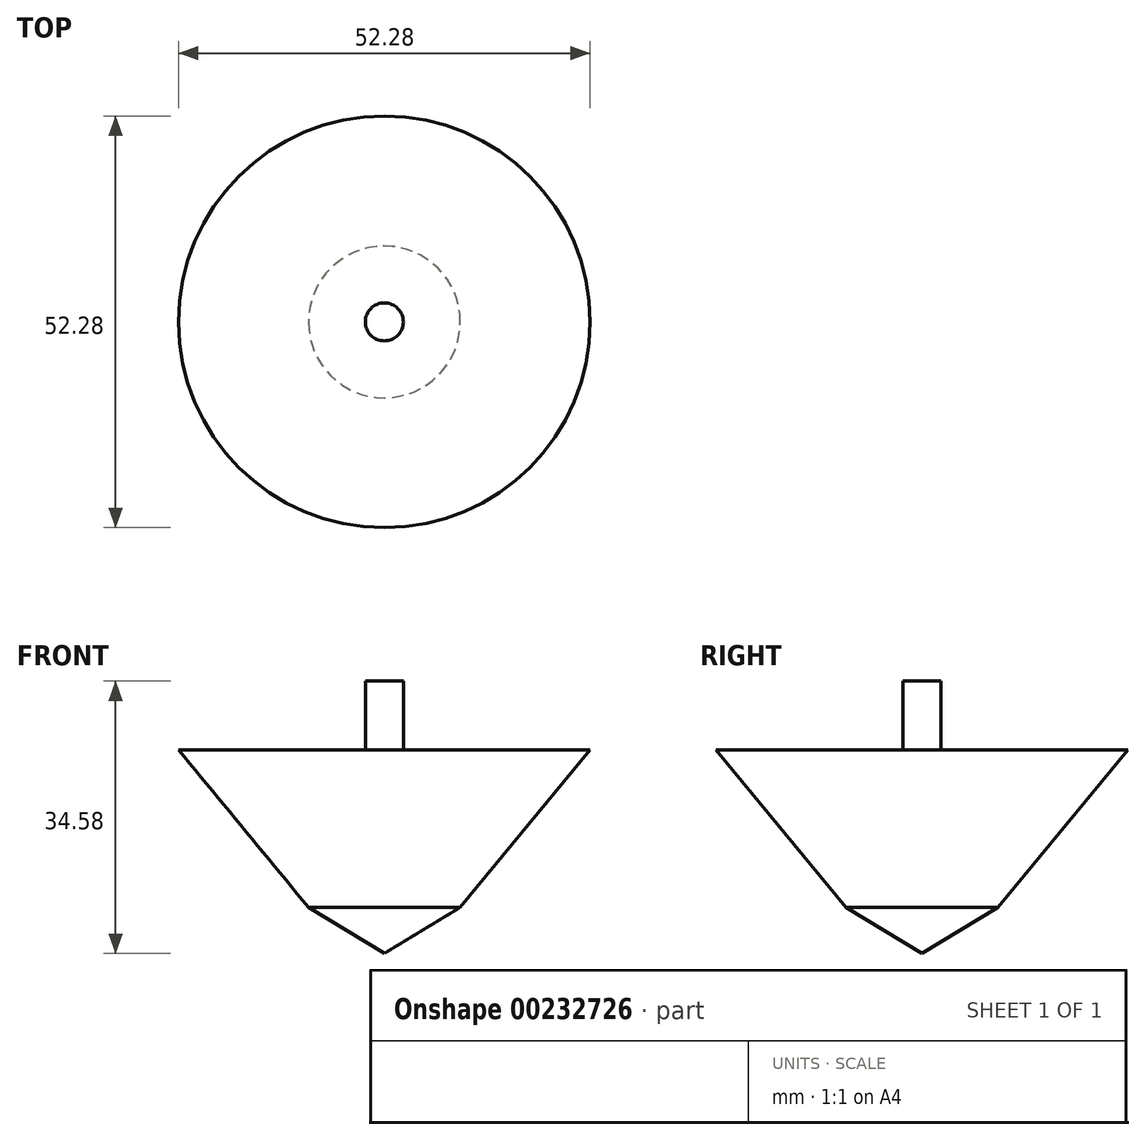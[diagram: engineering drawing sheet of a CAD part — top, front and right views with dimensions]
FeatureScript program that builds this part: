
annotation { "Feature Type Name" : "Feature", "Feature Type Description" : "" }
export const myFeature = defineFeature(function(context is Context, id is Id, definition is map)
    precondition{}
    {
        {
            var Q0;
            Q0=qCreatedBy(makeId("Front.planeOp"),FACE);
            var sketch = newSketch(context, id + "F0", { "sketchPlane" : qUnion([Q0])});
            skLineSegment(sketch, "E0", {"start": v(0, 0) * mm, "end": v(0, 34.58) * mm});
            skLineSegment(sketch, "E1", {"start": v(0, 34.58) * mm, "end": v(2.41, 34.58) * mm});
            skLineSegment(sketch, "E2", {"start": v(2.41, 34.58) * mm, "end": v(2.41, 25.87) * mm});
            skLineSegment(sketch, "E3", {"start": v(2.41, 25.87) * mm, "end": v(26.14, 25.87) * mm});
            skLineSegment(sketch, "E4", {"start": v(26.14, 25.87) * mm, "end": v(9.64, 5.84) * mm});
            skLineSegment(sketch, "E5", {"start": v(9.64, 5.84) * mm, "end": v(0, 0) * mm});
            skSolve(sketch);
        }
        {
            var Q0;
            Q0 = qSketchRegion(id + "F0", true);
            var Q1;
            Q1=sQuery(id+"F0.wireOp",EDGE,"E0");
            revolve(context, id + "F1", {"entities" : qUnion([Q0]), "axis" : qUnion([Q1]), "revolveType" : RevolveType.FULL});
        }
    });
